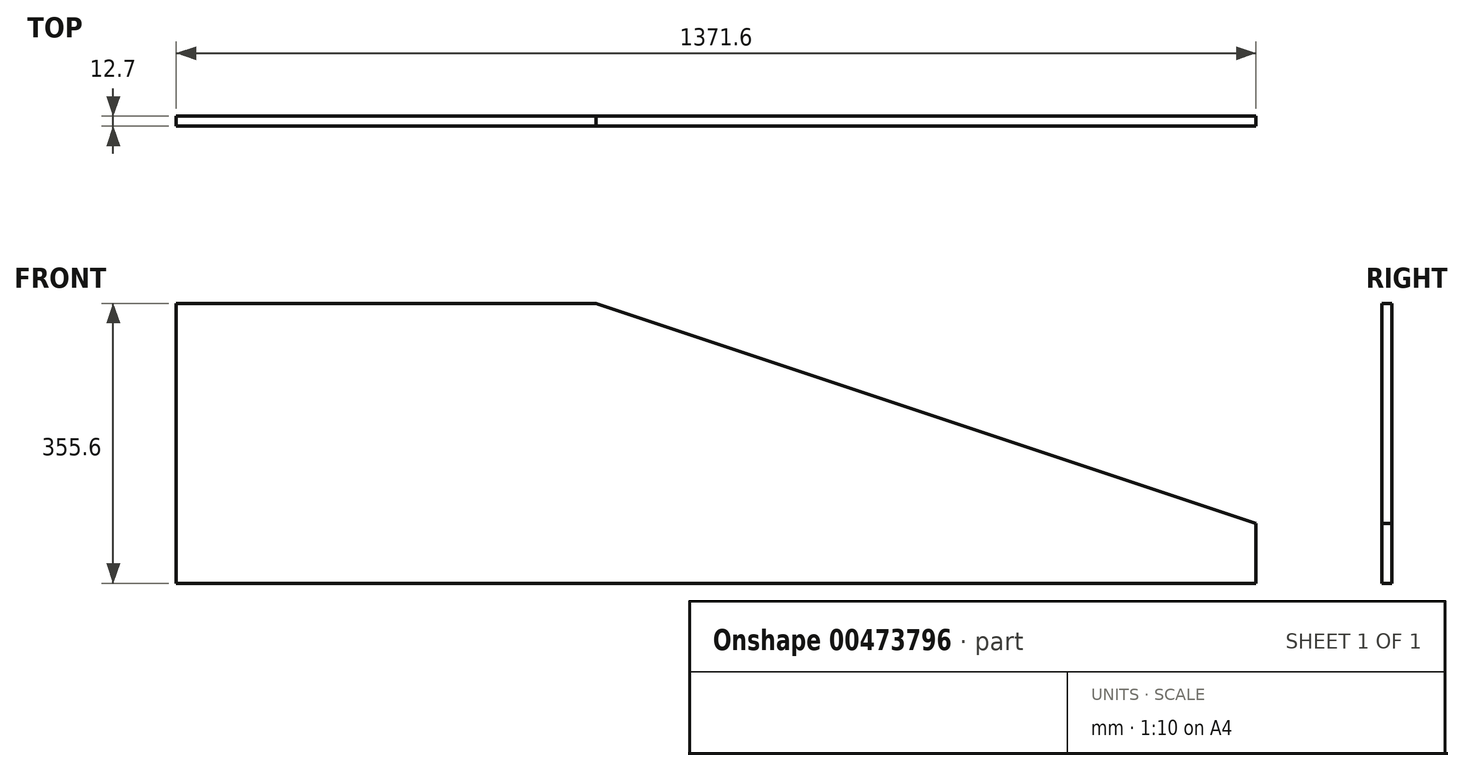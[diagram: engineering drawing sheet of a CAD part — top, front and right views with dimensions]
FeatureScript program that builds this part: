
annotation { "Feature Type Name" : "Feature", "Feature Type Description" : "" }
export const myFeature = defineFeature(function(context is Context, id is Id, definition is map)
    precondition{}
    {
        {
            var Q0;
            Q0=qCreatedBy(makeId("Front.planeOp"),FACE);
            var sketch = newSketch(context, id + "F0", { "sketchPlane" : qUnion([Q0])});
            skLineSegment(sketch, "E0", {"start": v(0, 0) * mm, "end": v(0, 355.6) * mm});
            skLineSegment(sketch, "E1", {"start": v(0, 355.6) * mm, "end": v(533.4, 355.6) * mm});
            skLineSegment(sketch, "E2", {"start": v(1371.6, 0) * mm, "end": v(0, 0) * mm});
            skLineSegment(sketch, "E3", {"start": v(1371.6, 0) * mm, "end": v(1371.6, 76.2) * mm});
            skLineSegment(sketch, "E4", {"start": v(1371.6, 76.2) * mm, "end": v(533.4, 355.6) * mm});
            skSolve(sketch);
        }
        {
            var Q0;
            Q0=makeQuery(id+"F0.imprint","IMPRINT",FACE,{"disambiguationData":[TD([[makeQuery(id+"F0.imprint","IMPRINT",EDGE,{"derivedFrom":sQuery(id+"F0.wireOp",EDGE,"E0")}),-1.0]])]});
            extrude(context, id + "F1", {"entities" : qUnion([Q0]), "depth" : 12.7 * mm, "offsetDistance" : 25.4 * mm});
        }
    });
